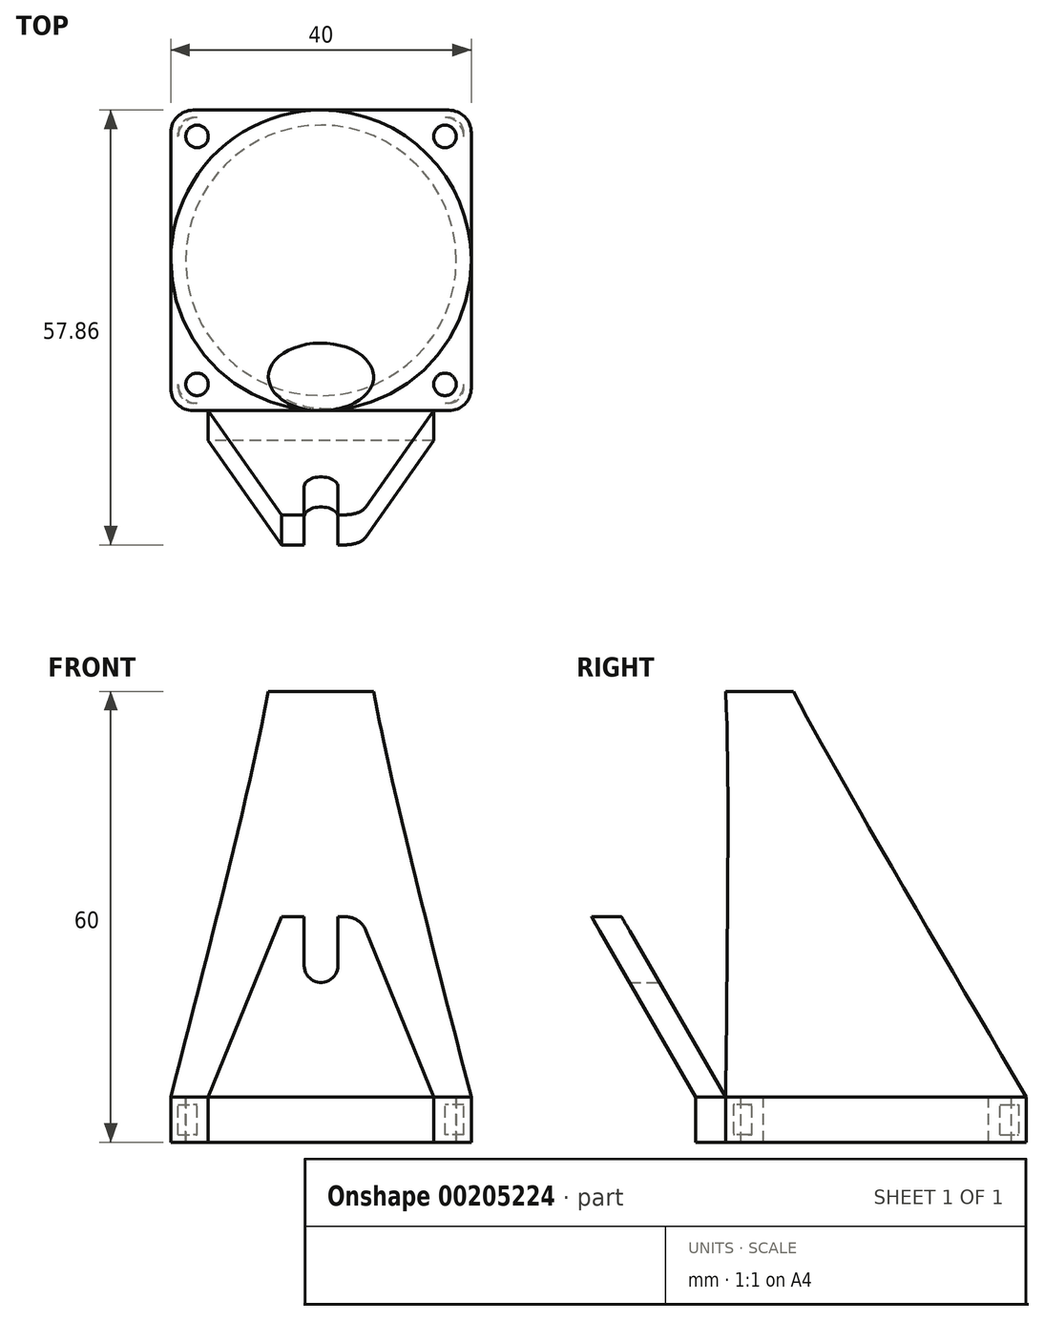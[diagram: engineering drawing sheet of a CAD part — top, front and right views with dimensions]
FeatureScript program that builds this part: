
annotation { "Feature Type Name" : "Feature", "Feature Type Description" : "" }
export const myFeature = defineFeature(function(context is Context, id is Id, definition is map)
    precondition{}
    {
        {
            var Q0;
            Q0=qCreatedBy(makeId("Top.planeOp"),FACE);
            var sketch = newSketch(context, id + "F0", { "sketchPlane" : qUnion([Q0])});
            skLineSegment(sketch, "E0.bottom", {"start": v(20, -20) * mm, "end": v(15, -20) * mm});
            skLineSegment(sketch, "E0.top", {"start": v(20, 20) * mm, "end": v(-20, 20) * mm});
            skLineSegment(sketch, "E0.left", {"start": v(20, -20) * mm, "end": v(20, 20) * mm});
            skLineSegment(sketch, "E0.right", {"start": v(-20, -20) * mm, "end": v(-20, 20) * mm});
            skPoint(sketch, "E0.middle", {"position": v(0, 0) * mm});
            skLineSegment(sketch, "E1.top", {"start": v(-15, -24) * mm, "end": v(15, -24) * mm});
            skLineSegment(sketch, "E1.left", {"start": v(-15, -20) * mm, "end": v(-15, -24) * mm});
            skLineSegment(sketch, "E1.right", {"start": v(15, -20) * mm, "end": v(15, -24) * mm});
            skLineSegment(sketch, "E2.trimOffspring", {"start": v(-15, -20) * mm, "end": v(-20, -20) * mm});
            skSolve(sketch);
        }
        {
            var Q0;
            Q0=makeQuery(id+"F0.imprint","IMPRINT",FACE,{"disambiguationData":[TD([[makeQuery(id+"F0.imprint","IMPRINT",EDGE,{"derivedFrom":sQuery(id+"F0.wireOp",EDGE,"E0.bottom")}),-1.0]])]});
            extrude(context, id + "F1", {"entities" : qUnion([Q0]), "depth" : 6 * mm});
        }
        {
            var Q0;
            Q0=qCreatedBy(makeId("Top.planeOp"),FACE);
            cPlane(context, id + "F2", {"entities" : qUnion([Q0]), "cplaneType" : CPlaneType.OFFSET, "offset" : 60 * mm, "width" : 150 * mm, "height" : 150 * mm});
        }
        {
            var Q0;
            Q0=qCreatedBy(id+"F2.planeOp",FACE);
            var sketch = newSketch(context, id + "F3", { "sketchPlane" : qUnion([Q0])});
            skLineSegment(sketch, "E3.0", {"start": v(20, -20) * mm, "end": v(20, -20) * mm});
            skEllipse(sketch, "E4", {"center": v(0, -15.5) * mm, "majorRadius": 7 * mm, "minorRadius": 4.5 * mm, "majorAxis": v(1, 0)});
            skPoint(sketch, "E4.centerSnap0", {"position": v(0, -20) * mm});
            skSolve(sketch);
        }
        {
            var Q0;
            Q0=makeQuery(id+"F1.opExtrude","CAP_FACE",FACE,{"disambiguationData":[OSD([sQuery(id+"F0.wireOp",EDGE,"E0.bottom"),sQuery(id+"F0.wireOp",EDGE,"E0.top"),sQuery(id+"F0.wireOp",EDGE,"E0.left"),sQuery(id+"F0.wireOp",EDGE,"E0.right")])],"isStart":false});
            var sketch = newSketch(context, id + "F4", { "sketchPlane" : qUnion([Q0])});
            skCircle(sketch, "E5", {"center": v(0, 0) * mm, "radius": 20 * mm});
            skSolve(sketch);
        }
        {
            var Q1;
            {var subQ0=sQuery(id+"F4.wireOp",EDGE,"E5");var subQ1=makeQuery(id+"F4.imprint","INTERSECT",VERTEX,{"derivedFrom":[makeQuery(id+"F1.opExtrude","CAP_EDGE",EDGE,{"disambiguationData":[OSD([sQuery(id+"F0.wireOp",EDGE,"E0.top")])],"isStart":false}),subQ0]});Q1=makeQuery(id+"F4.imprint","IMPRINT",FACE,{"disambiguationData":[TD([[makeQuery(id+"F4.imprint","IMPRINT",EDGE,{"disambiguationData":[TD([[subQ1,1.0]])],"derivedFrom":subQ0}),1.0]])]});}
            var Q2;
            Q2=makeQuery(id+"F3.imprint","IMPRINT",FACE,{"disambiguationData":[TD([[makeQuery(id+"F3.imprint","IMPRINT",EDGE,{"derivedFrom":sQuery(id+"F3.wireOp",EDGE,"E4")}),1.0]])]});
            loft(context, id + "F5", {"operationType" : NewBodyOperationType.ADD, "sheetProfilesArray" : [{ "sheetProfileEntities" : qUnion([Q1]) }, { "sheetProfileEntities" : qUnion([Q2]) }]});
        }
        {
            var Q0;
            Q0=qCreatedBy(makeId("Right.planeOp"),FACE);
            var sketch = newSketch(context, id + "F6", { "sketchPlane" : qUnion([Q0])});
            skLineSegment(sketch, "E6.0", {"start": v(-20, 6) * mm, "end": v(-24, 6) * mm});
            skLineSegment(sketch, "E7", {"start": v(-24, 6) * mm, "end": v(-37.86, 30) * mm});
            skLineSegment(sketch, "E8", {"start": v(-37.86, 30) * mm, "end": v(-33.86, 30) * mm});
            skLineSegment(sketch, "E9", {"start": v(-33.86, 30) * mm, "end": v(-20, 6) * mm});
            skSolve(sketch);
        }
        {
            var Q0;
            Q0=makeQuery(id+"F6.imprint","IMPRINT",FACE,{"disambiguationData":[TD([[makeQuery(id+"F6.imprint","IMPRINT",EDGE,{"derivedFrom":sQuery(id+"F6.wireOp",EDGE,"E6.0")}),-1.0]])]});
            var Q1;
            Q1=makeQuery(id+"F1.opExtrude","SWEPT_FACE",FACE,{"disambiguationData":[OSD([sQuery(id+"F0.wireOp",EDGE,"E1.right")])]});
            var Q2;
            Q2=makeQuery(id+"F1.opExtrude","SWEPT_FACE",FACE,{"disambiguationData":[OSD([sQuery(id+"F0.wireOp",EDGE,"E1.left")])]});
            extrude(context, id + "F7", {"entities" : qUnion([Q0]), "endBound" : BoundingType.UP_TO_SURFACE, "endBoundEntityFace" : qUnion([Q1]), "depth" : 25 * mm, "hasSecondDirection" : true, "secondDirectionBound" : SecondDirectionBoundingType.UP_TO_SURFACE, "secondDirectionOppositeDirection" : true, "secondDirectionBoundEntityFace" : qUnion([Q2]), "secondDirectionDepth" : 25 * mm});
        }
        {
            var Q0;
            Q0=qCreatedBy(makeId("Front.planeOp"),FACE);
            var sketch = newSketch(context, id + "F8", { "sketchPlane" : qUnion([Q0])});
            skLineSegment(sketch, "E10.0.0", {"start": v(-15, 6) * mm, "end": v(15, 6) * mm});
            skLineSegment(sketch, "E10.0.2", {"start": v(5.25, 30) * mm, "end": v(2.25, 30) * mm});
            skLineSegment(sketch, "E11", {"start": v(0, 30) * mm, "end": v(0, 23.5) * mm, "construction": true});
            skPoint(sketch, "E11.endSnap0", {"position": v(0, 30) * mm});
            skLineSegment(sketch, "E12.0", {"start": v(2.25, 30) * mm, "end": v(2.25, 23.5) * mm});
            skLineSegment(sketch, "E13.0", {"start": v(-2.25, 30) * mm, "end": v(-2.25, 23.5) * mm});
            skArc(sketch, "E14", {"start": v(-2.25, 23.5) * mm, "mid": v(0, 21.25) * mm, "end": v(2.25, 23.5) * mm});
            skLineSegment(sketch, "E15", {"start": v(-15, 6) * mm, "end": v(-5.25, 30) * mm});
            skLineSegment(sketch, "E16.MirrorCS", {"start": v(15, 6) * mm, "end": v(5.25, 30) * mm});
            skPoint(sketch, "E10.0.3.start.orphan", {"position": v(-15, 30) * mm});
            skPoint(sketch, "E10.0.1.end.orphan", {"position": v(15, 30) * mm});
            skLineSegment(sketch, "E17.trimOffspring", {"start": v(-2.25, 30) * mm, "end": v(-5.25, 30) * mm});
            skSolve(sketch);
        }
        {
            var Q0;
            Q0 = qSketchRegion(id + "F8", true);
            var Q1;
            Q1=makeQuery(id+"F7.opExtrude","SWEPT_FACE",FACE,{"disambiguationData":[OSD([sQuery(id+"F6.wireOp",EDGE,"E7")])]});
            var Q2;
            Q2=makeQuery(id+"F7.opExtrude","SWEPT_FACE",FACE,{"disambiguationData":[OSD([sQuery(id+"F6.wireOp",EDGE,"E9")])]});
            extrude(context, id + "F9", {"entities" : qUnion([Q0]), "endBound" : BoundingType.UP_TO_SURFACE, "endBoundEntityFace" : qUnion([Q1]), "depth" : 25 * mm});
        }
        {
            var Q0;
            Q0=makeQuery(id+"F7.opExtrude","SWEPT_BODY",BODY,{"disambiguationData":[OSD([sQuery(id+"F6.wireOp",EDGE,"E6.0"),sQuery(id+"F6.wireOp",EDGE,"E7"),sQuery(id+"F6.wireOp",EDGE,"E8"),sQuery(id+"F6.wireOp",EDGE,"E9")])]});
            var Q1;
            Q1=makeQuery(id+"F9.opExtrude","SWEPT_BODY",BODY,{"disambiguationData":[OSD([sQuery(id+"F8.wireOp",EDGE,"E10.0.0"),sQuery(id+"F8.wireOp",EDGE,"E10.0.2"),sQuery(id+"F8.wireOp",EDGE,"E12.0"),sQuery(id+"F8.wireOp",EDGE,"E13.0"),sQuery(id+"F8.wireOp",EDGE,"E14"),sQuery(id+"F8.wireOp",EDGE,"E15"),sQuery(id+"F8.wireOp",EDGE,"E16.MirrorCS"),sQuery(id+"F8.wireOp",EDGE,"E17.trimOffspring")])]});
            booleanBodies(context, id + "F10", {"operationType" : BooleanOperationType.INTERSECTION, "tools" : qUnion([Q0, Q1])});
        }
        {
            var Q0;
            Q0=makeQuery(id+"F1.opExtrude","CAP_FACE",FACE,{"disambiguationData":[OSD([sQuery(id+"F0.wireOp",EDGE,"E0.bottom"),sQuery(id+"F0.wireOp",EDGE,"E0.top"),sQuery(id+"F0.wireOp",EDGE,"E0.left"),sQuery(id+"F0.wireOp",EDGE,"E0.right"),sQuery(id+"F0.wireOp",EDGE,"E1.top"),sQuery(id+"F0.wireOp",EDGE,"E1.left"),sQuery(id+"F0.wireOp",EDGE,"E1.right"),sQuery(id+"F0.wireOp",EDGE,"E2.trimOffspring")])],"isStart":true});
            var sketch = newSketch(context, id + "F11", { "sketchPlane" : qUnion([Q0])});
            skCircle(sketch, "E18", {"center": v(0, 0) * mm, "radius": 18 * mm});
            skSolve(sketch);
        }
        {
            var Q0;
            Q0=makeQuery(id+"F11.imprint","IMPRINT",FACE,{"disambiguationData":[TD([[makeQuery(id+"F11.imprint","IMPRINT",EDGE,{"derivedFrom":sQuery(id+"F11.wireOp",EDGE,"E18")}),1.0]])]});
            extrude(context, id + "F12", {"entities" : qUnion([Q0]), "operationType" : NewBodyOperationType.REMOVE, "oppositeDirection" : true, "depth" : 6 * mm});
        }
        {
            var Q0;
            {var subQ0=sQuery(id+"F0.wireOp",EDGE,"E0.right");var subQ1=sQuery(id+"F0.wireOp",EDGE,"E0.top");var subQ2=makeQuery(id+"F1.opExtrude","CAP_FACE",FACE,{"disambiguationData":[OSD([sQuery(id+"F0.wireOp",EDGE,"E0.bottom"),subQ1,sQuery(id+"F0.wireOp",EDGE,"E0.left"),subQ0,sQuery(id+"F0.wireOp",EDGE,"E1.top"),sQuery(id+"F0.wireOp",EDGE,"E1.left"),sQuery(id+"F0.wireOp",EDGE,"E1.right"),sQuery(id+"F0.wireOp",EDGE,"E2.trimOffspring")])],"isStart":false});Q0=makeQuery(id+"F5.boolean.opBoolean","SPLIT",FACE,{"disambiguationData":[TD([subQ2,makeQuery(id+"F1.opExtrude","SWEPT_FACE",FACE,{"disambiguationData":[OSD([subQ1])]}),makeQuery(id+"F1.opExtrude","SWEPT_FACE",FACE,{"disambiguationData":[OSD([subQ0])]}),makeQuery(id+"F5.opLoft","SWEPT_FACE",FACE,{"disambiguationData":[OSD([subQ1,subQ0,sQuery(id+"F3.wireOp",EDGE,"E4"),sQuery(id+"F4.wireOp",EDGE,"E5")])]})])],"derivedFrom":subQ2});}
            var sketch = newSketch(context, id + "F13", { "sketchPlane" : qUnion([Q0])});
            skLineSegment(sketch, "E19.bottom", {"start": v(-16.5, 16.5) * mm, "end": v(16.5, 16.5) * mm, "construction": true});
            skLineSegment(sketch, "E19.top", {"start": v(-16.5, -16.5) * mm, "end": v(16.5, -16.5) * mm, "construction": true});
            skLineSegment(sketch, "E19.left", {"start": v(-16.5, 16.5) * mm, "end": v(-16.5, -16.5) * mm, "construction": true});
            skLineSegment(sketch, "E19.right", {"start": v(16.5, 16.5) * mm, "end": v(16.5, -16.5) * mm, "construction": true});
            skCircle(sketch, "E20", {"center": v(-16.5, 16.5) * mm, "radius": 1.5 * mm});
            skCircle(sketch, "E21.0.1.0", {"center": v(-16.5, -16.5) * mm, "radius": 1.5 * mm});
            skCircle(sketch, "E21.1.0.0", {"center": v(16.5, 16.5) * mm, "radius": 1.5 * mm});
            skCircle(sketch, "E21.1.1.0", {"center": v(16.5, -16.5) * mm, "radius": 1.5 * mm});
            skSolve(sketch);
        }
        {
            var Q0;
            Q0 = qSketchRegion(id + "F13", true);
            extrude(context, id + "F14", {"entities" : qUnion([Q0]), "operationType" : NewBodyOperationType.REMOVE, "endBound" : BoundingType.UP_TO_NEXT, "oppositeDirection" : true, "depth" : 25 * mm});
        }
        {
            var Q0;
            Q0=makeQuery(id+"F1.opExtrude","SWEPT_EDGE",EDGE,{"disambiguationData":[OSD([sQuery(id+"F0.wireOp",EDGE,"E0.right"),sQuery(id+"F0.wireOp",EDGE,"E2.trimOffspring")])]});
            var Q1;
            Q1=makeQuery(id+"F1.opExtrude","SWEPT_EDGE",EDGE,{"disambiguationData":[OSD([sQuery(id+"F0.wireOp",EDGE,"E0.bottom"),sQuery(id+"F0.wireOp",EDGE,"E0.left")])]});
            var Q2;
            Q2=makeQuery(id+"F1.opExtrude","SWEPT_EDGE",EDGE,{"disambiguationData":[OSD([sQuery(id+"F0.wireOp",EDGE,"E0.top"),sQuery(id+"F0.wireOp",EDGE,"E0.right")])]});
            var Q3;
            Q3=makeQuery(id+"F1.opExtrude","SWEPT_EDGE",EDGE,{"disambiguationData":[OSD([sQuery(id+"F0.wireOp",EDGE,"E0.top"),sQuery(id+"F0.wireOp",EDGE,"E0.left")])]});
            var Q4;
            Q4=makeQuery(id+"F9.opExtrude","SWEPT_EDGE",EDGE,{"disambiguationData":[OSD([sQuery(id+"F8.wireOp",EDGE,"E15"),sQuery(id+"F8.wireOp",EDGE,"E17.trimOffspring")])]});
            var Q5;
            Q5=makeQuery(id+"F9.opExtrude","SWEPT_EDGE",EDGE,{"disambiguationData":[OSD([sQuery(id+"F8.wireOp",EDGE,"E10.0.2"),sQuery(id+"F8.wireOp",EDGE,"E16.MirrorCS")])]});
            fillet(context, id + "F15", {"entities" : qUnion([Q0, Q1, Q2, Q3, Q4, Q5]), "radius" : 3 * mm, "tangentPropagation" : true, "allowEdgeOverflow" : false});
        }
        {
            var Q0;
            Q0=makeQuery(id+"F5.opLoft","CAP_FACE",FACE,{"disambiguationData":[OSD([makeQuery(id+"F3.imprint","IMPRINT",FACE,{"disambiguationData":[TD([[makeQuery(id+"F3.imprint","IMPRINT",EDGE,{"derivedFrom":sQuery(id+"F3.wireOp",EDGE,"E4")}),1.0]])]})])],"isStart":true});
            var Q1;
            Q1=makeQuery(id+"F12.boolean.opBoolean","COPY",FACE,{"derivedFrom":makeQuery(id+"F12.opExtrude","CAP_FACE",FACE,{"disambiguationData":[OSD([sQuery(id+"F11.wireOp",EDGE,"E18")])],"isStart":false})});
            shell(context, id + "F16", {"entities" : qUnion([Q0, Q1]), "thickness" : 1 * mm});
        }
    });
